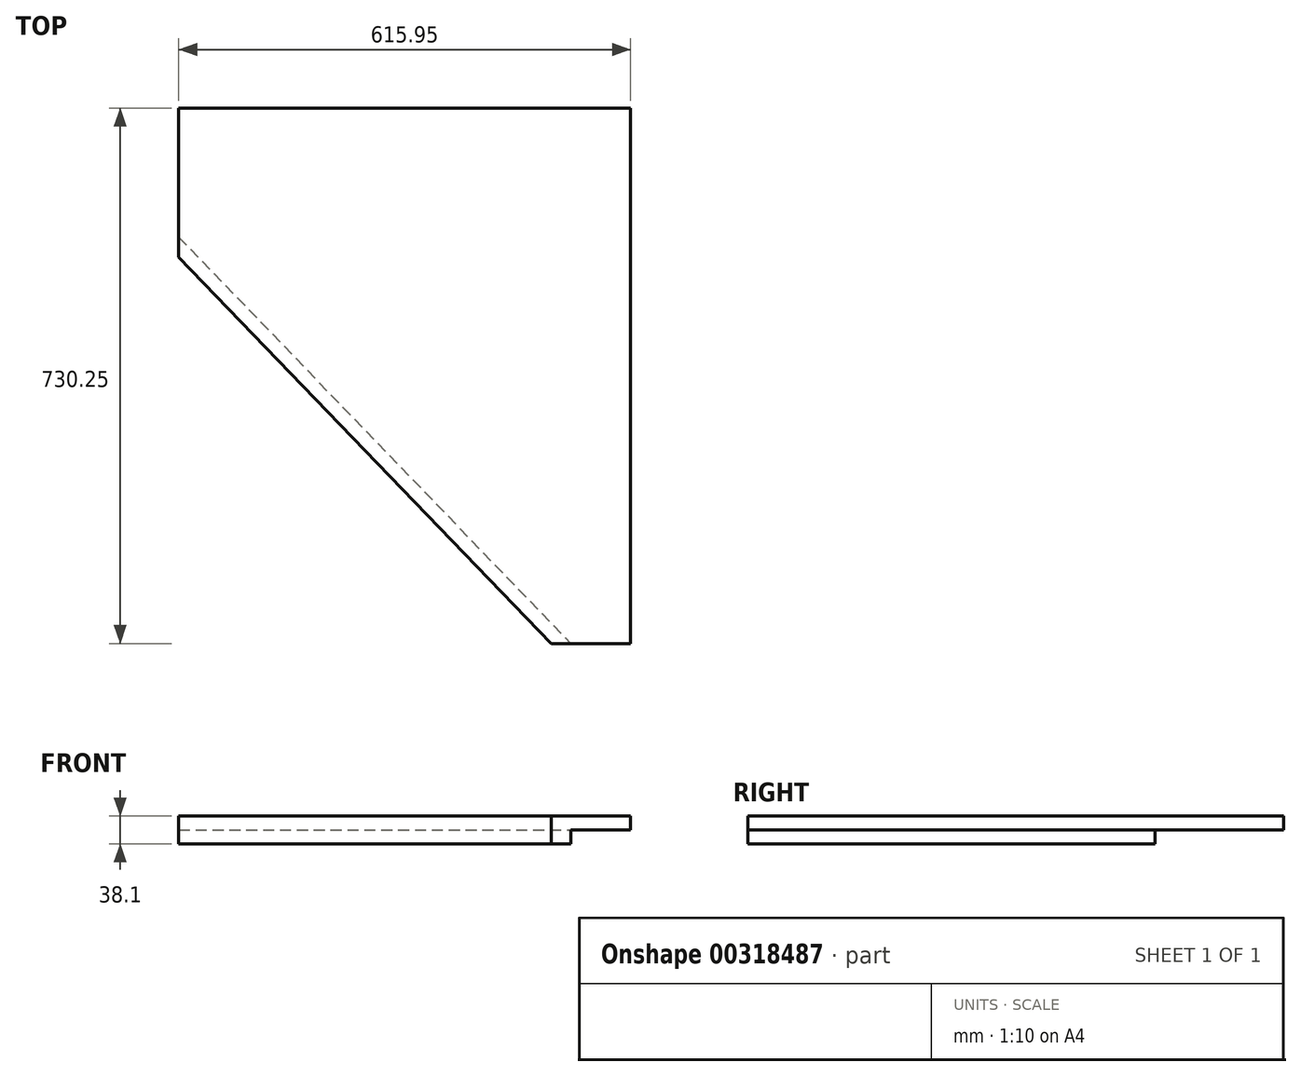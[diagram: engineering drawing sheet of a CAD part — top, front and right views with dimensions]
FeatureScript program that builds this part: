
annotation { "Feature Type Name" : "Feature", "Feature Type Description" : "" }
export const myFeature = defineFeature(function(context is Context, id is Id, definition is map)
    precondition{}
    {
        {
            var Q0;
            Q0=qCreatedBy(makeId("Top.planeOp"),FACE);
            var sketch = newSketch(context, id + "F0", { "sketchPlane" : qUnion([Q0])});
            skLineSegment(sketch, "E0.bottom", {"start": v(-334.3, 545.33) * mm, "end": v(281.66, 545.33) * mm});
            skLineSegment(sketch, "E0.top", {"start": v(173.7, -184.92) * mm, "end": v(281.66, -184.92) * mm});
            skLineSegment(sketch, "E0.left", {"start": v(-334.3, 545.33) * mm, "end": v(-334.3, 342.13) * mm});
            skLineSegment(sketch, "E0.right", {"start": v(281.66, 545.33) * mm, "end": v(281.66, -184.92) * mm});
            skLineSegment(sketch, "E1", {"start": v(-334.3, 342.13) * mm, "end": v(173.7, -184.92) * mm});
            skSolve(sketch);
        }
        {
            var Q0;
            Q0=makeQuery(id+"F0.imprint","IMPRINT",FACE,{"disambiguationData":[TD([[makeQuery(id+"F0.imprint","IMPRINT",EDGE,{"derivedFrom":sQuery(id+"F0.wireOp",EDGE,"E0.bottom")}),-1.0]])]});
            extrude(context, id + "F1", {"entities" : qUnion([Q0]), "depth" : 19.05 * mm});
        }
        {
            var Q0;
            Q0=makeQuery(id+"F1.opExtrude","CAP_FACE",FACE,{"disambiguationData":[OSD([sQuery(id+"F0.wireOp",EDGE,"E0.bottom"),sQuery(id+"F0.wireOp",EDGE,"E0.top"),sQuery(id+"F0.wireOp",EDGE,"E0.left"),sQuery(id+"F0.wireOp",EDGE,"E0.right"),sQuery(id+"F0.wireOp",EDGE,"E1")])],"isStart":true});
            var sketch = newSketch(context, id + "F2", { "sketchPlane" : qUnion([Q0])});
            skLineSegment(sketch, "E2.0", {"start": v(-381.64, -418.71) * mm, "end": v(219.87, 205.36) * mm});
            skSolve(sketch);
        }
        {
            var Q0;
            {var subQ5=makeQuery(id+"F1.opExtrude","CAP_EDGE",EDGE,{"disambiguationData":[OSD([sQuery(id+"F0.wireOp",EDGE,"E1")])],"isStart":true});Q0=makeQuery(id+"F2.imprint","IMPRINT",FACE,{"disambiguationData":[TD([[makeQuery(id+"F2.imprint","IMPRINT",EDGE,{"derivedFrom":subQ5}),-1.0]])]});}
            extrude(context, id + "F3", {"entities" : qUnion([Q0]), "operationType" : NewBodyOperationType.ADD, "depth" : 19.05 * mm});
        }
    });
